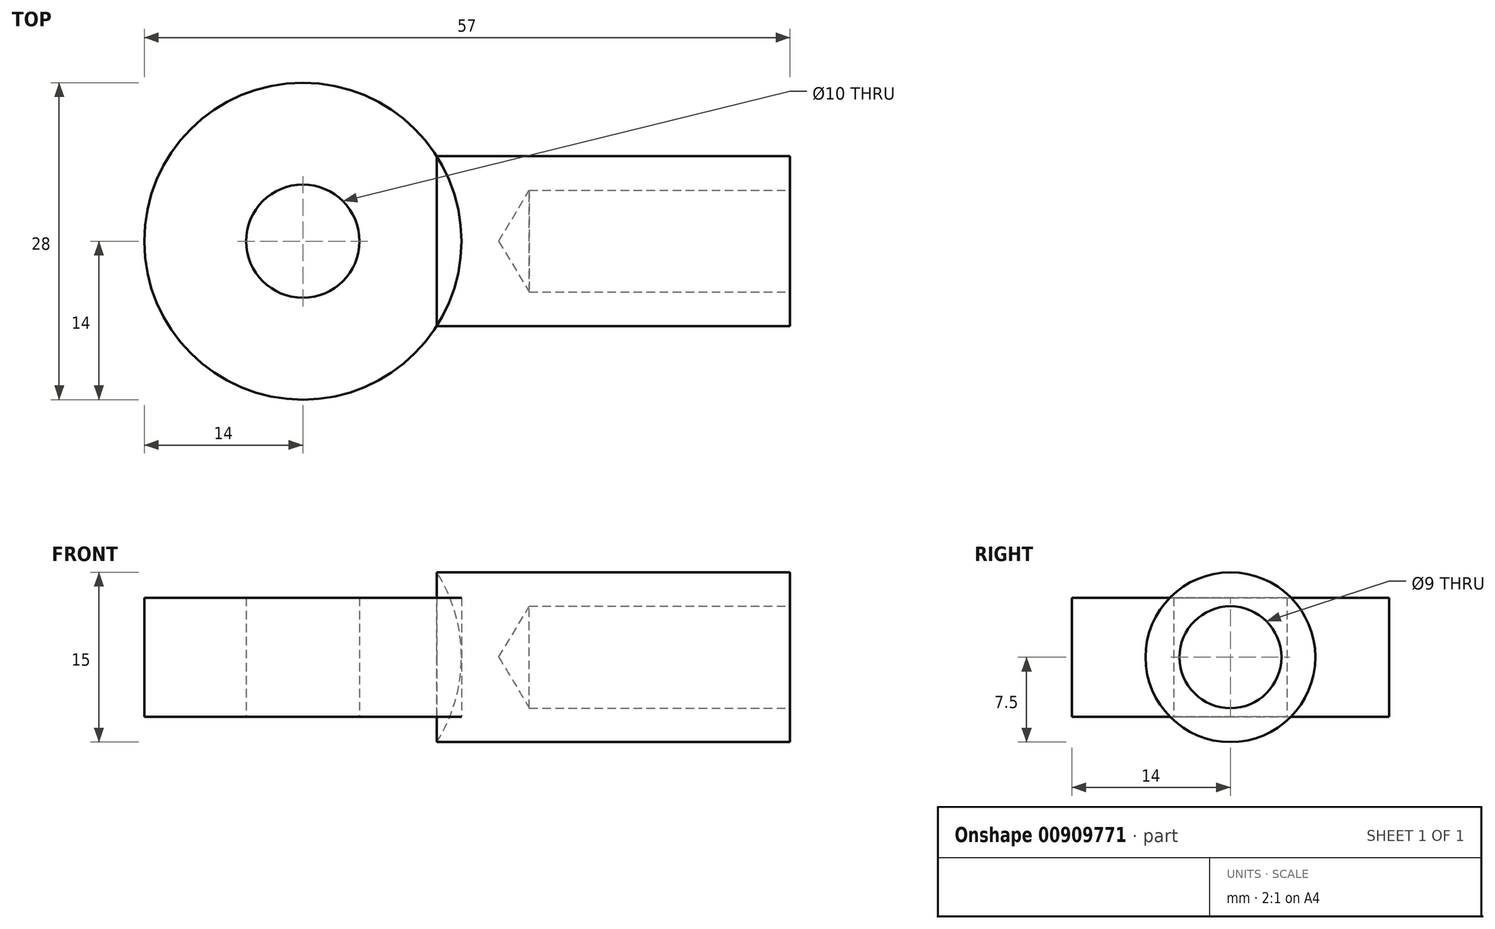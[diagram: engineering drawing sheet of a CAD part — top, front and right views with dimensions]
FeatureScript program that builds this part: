
annotation { "Feature Type Name" : "Feature", "Feature Type Description" : "" }
export const myFeature = defineFeature(function(context is Context, id is Id, definition is map)
    precondition{}
    {
        {
            var Q0;
            Q0=qCreatedBy(makeId("Top.planeOp"),FACE);
            var sketch = newSketch(context, id + "F0", { "sketchPlane" : qUnion([Q0])});
            skCircle(sketch, "E0", {"center": v(0, 0) * mm, "radius": 5 * mm});
            skCircle(sketch, "E1", {"center": v(0, 0) * mm, "radius": 14 * mm});
            skLineSegment(sketch, "E2.top", {"start": v(11.82, 7.5) * mm, "end": v(43, 7.5) * mm});
            skLineSegment(sketch, "E3.MirrorCS", {"start": v(11.82, -7.5) * mm, "end": v(43, -7.5) * mm});
            skLineSegment(sketch, "E4", {"start": v(43, 7.5) * mm, "end": v(43, -7.5) * mm});
            skLineSegment(sketch, "E5", {"start": v(0, 0) * mm, "end": v(52.44, 0) * mm, "construction": true});
            skLineSegment(sketch, "E6", {"start": v(52.44, 0) * mm, "end": v(-15.22, 0) * mm, "construction": true});
            skLineSegment(sketch, "E7", {"start": v(43, 0) * mm, "end": v(14, 0) * mm});
            skSolve(sketch);
        }
        {
            var Q0;
            Q0=makeQuery(id+"F0.imprint","IMPRINT",FACE,{"disambiguationData":[TD([[makeQuery(id+"F0.imprint","IMPRINT",EDGE,{"derivedFrom":sQuery(id+"F0.wireOp",EDGE,"E0")}),-1.0]])]});
            extrude(context, id + "F1", {"entities" : qUnion([Q0]), "endBound" : BoundingType.SYMMETRIC, "depth" : 10.5 * mm, "offsetDistance" : 25 * mm});
        }
        {
            var Q0;
            {var subQ0=sQuery(id+"F0.wireOp",EDGE,"E2.top");Q0=makeQuery(id+"F0.imprint","IMPRINT",FACE,{"disambiguationData":[TD([[makeQuery(id+"F0.imprint","IMPRINT",EDGE,{"derivedFrom":subQ0}),-1.0]])]});}
            var Q1;
            Q1=sQuery(id+"F0.wireOp",EDGE,"E6");
            revolve(context, id + "F2", {"surfaceOperationType" : NewSurfaceOperationType.NEW, "entities" : qUnion([Q0]), "axis" : qUnion([Q1]), "revolveType" : RevolveType.FULL});
        }
        {
            var Q0;
            Q0=makeQuery(id+"F2.opRevolve","SWEPT_FACE",FACE,{"disambiguationData":[OSD([sQuery(id+"F0.wireOp",EDGE,"E4")])]});
            var sketch = newSketch(context, id + "F3", { "sketchPlane" : qUnion([Q0])});
            skPoint(sketch, "E8", {"position": v(0, 0) * mm});
            skSolve(sketch);
        }
        {
            var Q0;
            Q0=sQuery(id+"F3.wireOp",VERTEX,"E8");
            var Q1;
            Q1=makeQuery(id+"F2.opRevolve","SWEPT_BODY",BODY,{"disambiguationData":[OSD([sQuery(id+"F0.wireOp",EDGE,"E1"),sQuery(id+"F0.wireOp",EDGE,"E2.top"),sQuery(id+"F0.wireOp",EDGE,"E4"),sQuery(id+"F0.wireOp",EDGE,"E7")])]});
            hole(context, id + "F4", {"style" : HoleStyle.SIMPLE, "endStyle" : HoleEndStyle.BLIND, "standardTappedOrClearance" : lookupTablePath({ "standard" : "ISO", "engagement" : "75%", "pitch" : "1 mm", "size" : "M10", "type" : "Tapped" }), "standardBlindInLast" : lookupTablePath({ "standard" : "ISO", "engagement" : "75%", "pitch" : "1 mm", "size" : "M10", "type" : "Tapped" }), "holeDiameter" : 9 * mm, "majorDiameter" : 10 * mm, "showTappedDepth" : true, "holeDepth" : 23 * mm, "isTappedThrough" : true, "tappedDepth" : 20 * mm, "tapClearance" : 3, "startFromSketch" : true, "locations" : qUnion([Q0]), "scope" : qUnion([Q1])});
        }
    });
